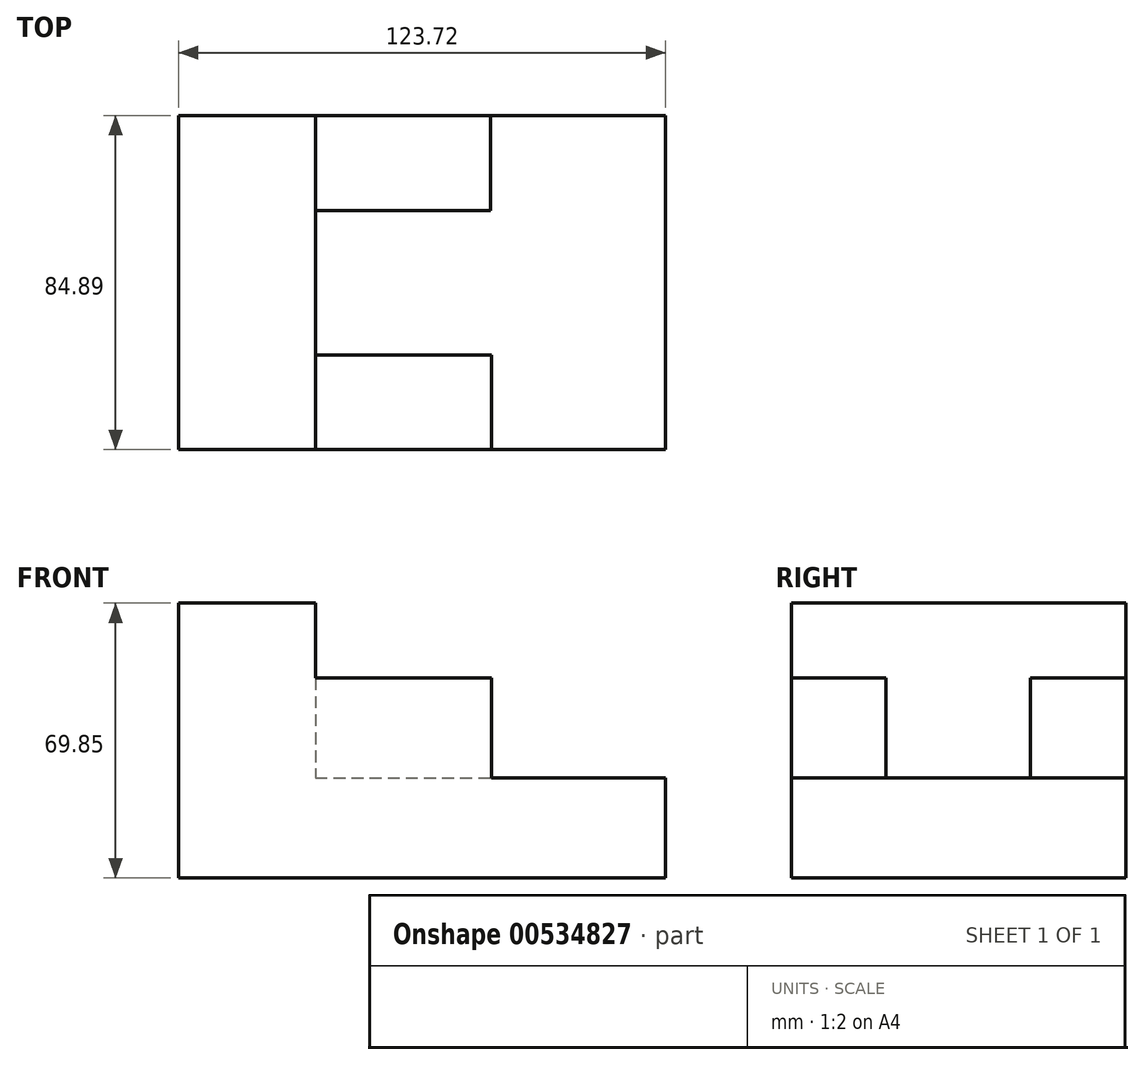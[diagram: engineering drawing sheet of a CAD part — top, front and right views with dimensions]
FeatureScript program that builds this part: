
annotation { "Feature Type Name" : "Feature", "Feature Type Description" : "" }
export const myFeature = defineFeature(function(context is Context, id is Id, definition is map)
    precondition{}
    {
        {
            var Q0;
            Q0=qCreatedBy(makeId("Top.planeOp"),FACE);
            var sketch = newSketch(context, id + "F0", { "sketchPlane" : qUnion([Q0])});
            skLineSegment(sketch, "E0.bottom", {"start": v(-20.32, 42.67) * mm, "end": v(103.4, 42.67) * mm});
            skLineSegment(sketch, "E0.top", {"start": v(-20.32, -42.22) * mm, "end": v(103.4, -42.22) * mm});
            skLineSegment(sketch, "E0.left", {"start": v(-20.32, 42.67) * mm, "end": v(-20.32, -42.22) * mm});
            skLineSegment(sketch, "E0.right", {"start": v(103.4, 42.67) * mm, "end": v(103.4, -42.22) * mm});
            skSolve(sketch);
        }
        {
            var Q0;
            Q0=makeQuery(id+"F0.imprint","IMPRINT",FACE,{"disambiguationData":[TD([[makeQuery(id+"F0.imprint","IMPRINT",EDGE,{"derivedFrom":sQuery(id+"F0.wireOp",EDGE,"E0.bottom")}),-1.0]])]});
            extrude(context, id + "F1", {"entities" : qUnion([Q0]), "depth" : 25.4 * mm, "offsetDistance" : 25.4 * mm});
        }
        {
            var Q0;
            Q0=makeQuery(id+"F1.opExtrude","CAP_FACE",FACE,{"disambiguationData":[OSD([sQuery(id+"F0.wireOp",EDGE,"E0.bottom"),sQuery(id+"F0.wireOp",EDGE,"E0.top"),sQuery(id+"F0.wireOp",EDGE,"E0.left"),sQuery(id+"F0.wireOp",EDGE,"E0.right")])],"isStart":false});
            var sketch = newSketch(context, id + "F2", { "sketchPlane" : qUnion([Q0])});
            skLineSegment(sketch, "E1.bottom", {"start": v(14.45, -42.22) * mm, "end": v(-20.32, -42.22) * mm});
            skLineSegment(sketch, "E1.top", {"start": v(14.45, 42.67) * mm, "end": v(-20.32, 42.67) * mm});
            skLineSegment(sketch, "E1.left", {"start": v(14.45, -42.22) * mm, "end": v(14.45, 42.67) * mm});
            skLineSegment(sketch, "E1.right", {"start": v(-20.32, -42.22) * mm, "end": v(-20.32, 42.67) * mm});
            skSolve(sketch);
        }
        {
            var Q0;
            Q0=makeQuery(id+"F2.imprint","IMPRINT",FACE,{"disambiguationData":[TD([[makeQuery(id+"F2.imprint","IMPRINT",EDGE,{"derivedFrom":sQuery(id+"F2.wireOp",EDGE,"E1.bottom")}),1.0]])]});
            extrude(context, id + "F3", {"entities" : qUnion([Q0]), "operationType" : NewBodyOperationType.ADD, "depth" : 44.45 * mm, "offsetDistance" : 25.4 * mm});
        }
        {
            var Q0;
            Q0=makeQuery(id+"F1.opExtrude","CAP_FACE",FACE,{"disambiguationData":[OSD([sQuery(id+"F0.wireOp",EDGE,"E0.bottom"),sQuery(id+"F0.wireOp",EDGE,"E0.top"),sQuery(id+"F0.wireOp",EDGE,"E0.left"),sQuery(id+"F0.wireOp",EDGE,"E0.right")])],"isStart":false});
            var sketch = newSketch(context, id + "F4", { "sketchPlane" : qUnion([Q0])});
            skLineSegment(sketch, "E2.bottom", {"start": v(14.45, -42.22) * mm, "end": v(59.17, -42.22) * mm});
            skLineSegment(sketch, "E2.top", {"start": v(14.45, -18.17) * mm, "end": v(59.17, -18.17) * mm});
            skLineSegment(sketch, "E2.left", {"start": v(14.45, -42.22) * mm, "end": v(14.45, -18.17) * mm});
            skLineSegment(sketch, "E2.right", {"start": v(59.17, -42.22) * mm, "end": v(59.17, -18.17) * mm});
            skSolve(sketch);
        }
        {
            var Q0;
            Q0=makeQuery(id+"F4.imprint","IMPRINT",FACE,{"disambiguationData":[TD([[makeQuery(id+"F4.imprint","IMPRINT",EDGE,{"derivedFrom":sQuery(id+"F4.wireOp",EDGE,"E2.bottom")}),1.0]])]});
            extrude(context, id + "F5", {"entities" : qUnion([Q0]), "operationType" : NewBodyOperationType.ADD, "depth" : 25.4 * mm, "offsetDistance" : 25.4 * mm});
        }
        {
            var Q0;
            Q0=makeQuery(id+"F1.opExtrude","CAP_FACE",FACE,{"disambiguationData":[OSD([sQuery(id+"F0.wireOp",EDGE,"E0.bottom"),sQuery(id+"F0.wireOp",EDGE,"E0.top"),sQuery(id+"F0.wireOp",EDGE,"E0.left"),sQuery(id+"F0.wireOp",EDGE,"E0.right")])],"isStart":false});
            var sketch = newSketch(context, id + "F6", { "sketchPlane" : qUnion([Q0])});
            skLineSegment(sketch, "E3.bottom", {"start": v(14.45, 18.48) * mm, "end": v(58.92, 18.48) * mm});
            skLineSegment(sketch, "E3.top", {"start": v(14.45, 42.67) * mm, "end": v(58.92, 42.67) * mm});
            skLineSegment(sketch, "E3.left", {"start": v(14.45, 18.48) * mm, "end": v(14.45, 42.67) * mm});
            skLineSegment(sketch, "E3.right", {"start": v(58.92, 18.48) * mm, "end": v(58.92, 42.67) * mm});
            skSolve(sketch);
        }
        {
            var Q0;
            Q0=makeQuery(id+"F6.imprint","IMPRINT",FACE,{"disambiguationData":[TD([[makeQuery(id+"F6.imprint","IMPRINT",EDGE,{"derivedFrom":sQuery(id+"F6.wireOp",EDGE,"E3.bottom")}),1.0]])]});
            extrude(context, id + "F7", {"entities" : qUnion([Q0]), "operationType" : NewBodyOperationType.ADD, "depth" : 25.4 * mm, "offsetDistance" : 25.4 * mm});
        }
    });
